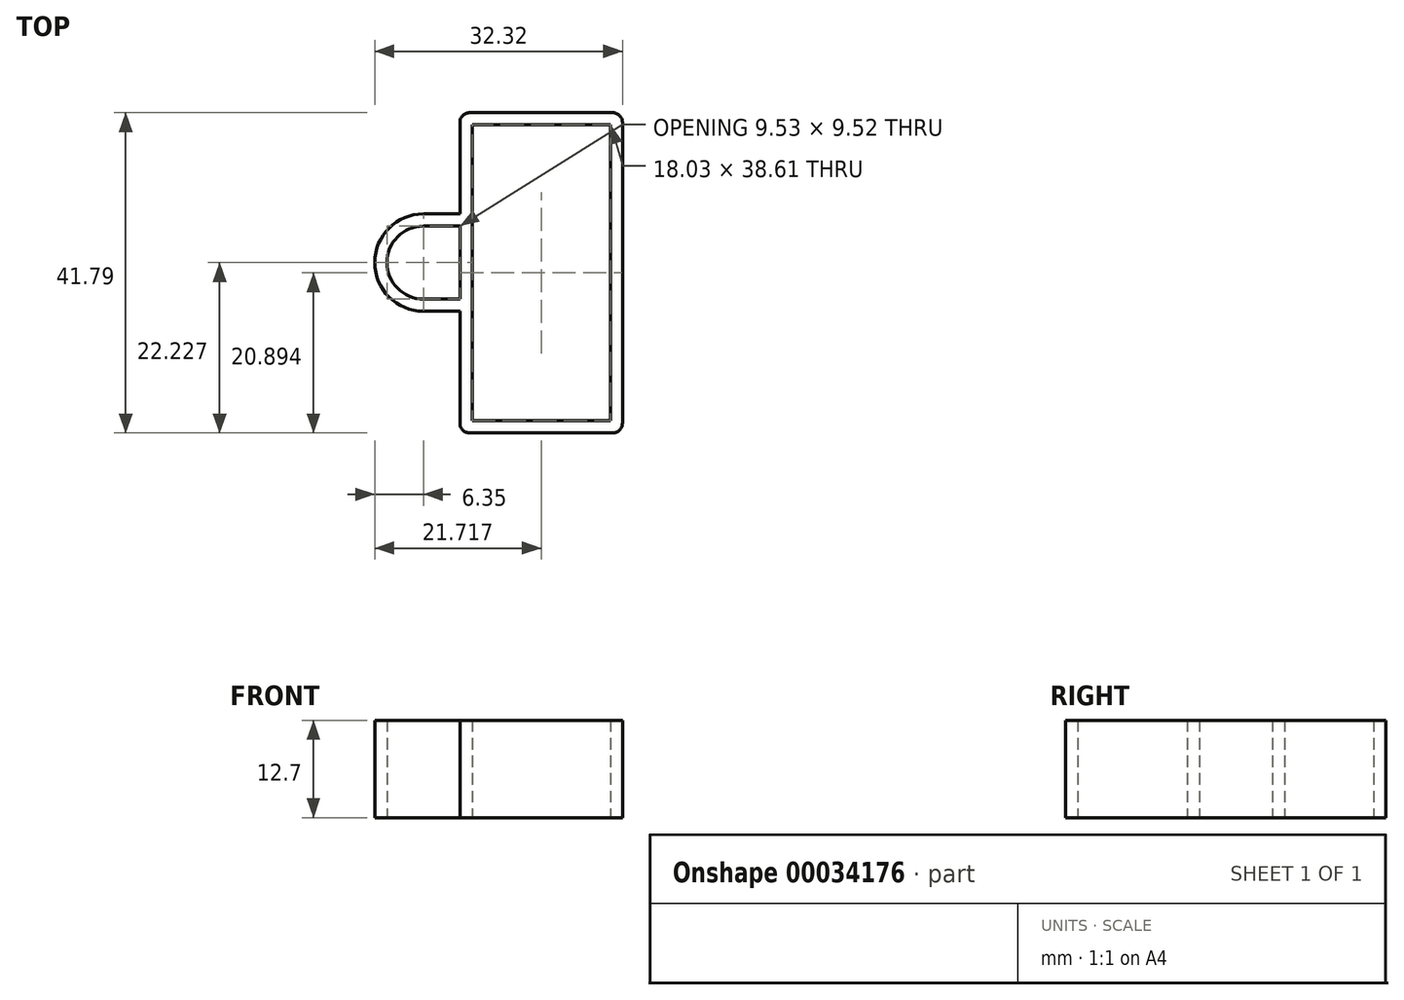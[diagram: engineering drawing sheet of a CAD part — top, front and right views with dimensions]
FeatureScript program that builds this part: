
annotation { "Feature Type Name" : "Feature", "Feature Type Description" : "" }
export const myFeature = defineFeature(function(context is Context, id is Id, definition is map)
    precondition{}
    {
        {
            var Q0;
            Q0=qCreatedBy(makeId("Top.planeOp"),FACE);
            var sketch = newSketch(context, id + "F0", { "sketchPlane" : qUnion([Q0])});
            skLineSegment(sketch, "E0.bottom", {"start": v(0, 0) * mm, "end": v(18.03, 0) * mm});
            skLineSegment(sketch, "E0.top", {"start": v(0, 38.6) * mm, "end": v(18.03, 38.6) * mm});
            skLineSegment(sketch, "E0.left", {"start": v(0, 0) * mm, "end": v(0, 38.6) * mm});
            skLineSegment(sketch, "E0.right", {"start": v(18.03, 0) * mm, "end": v(18.03, 38.6) * mm});
            skLineSegment(sketch, "E1.0", {"start": v(-1.59, -1.59) * mm, "end": v(-1.59, 40.2) * mm});
            skLineSegment(sketch, "E1.1", {"start": v(-1.59, -1.59) * mm, "end": v(19.62, -1.59) * mm});
            skLineSegment(sketch, "E1.2", {"start": v(19.62, -1.59) * mm, "end": v(19.62, 40.2) * mm});
            skLineSegment(sketch, "E1.3", {"start": v(-1.59, 40.2) * mm, "end": v(19.62, 40.2) * mm});
            skArc(sketch, "E2", {"start": v(-6.35, 25.4) * mm, "mid": v(-11.11, 20.64) * mm, "end": v(-6.35, 15.88) * mm});
            skLineSegment(sketch, "E3", {"start": v(-1.59, 25.4) * mm, "end": v(-6.35, 25.4) * mm});
            skLineSegment(sketch, "E4", {"start": v(-1.59, 15.88) * mm, "end": v(-6.35, 15.88) * mm});
            skLineSegment(sketch, "E5.0", {"start": v(-1.59, 14.29) * mm, "end": v(-6.35, 14.29) * mm});
            skArc(sketch, "E5.1", {"start": v(-6.35, 26.99) * mm, "mid": v(-12.7, 20.64) * mm, "end": v(-6.35, 14.29) * mm});
            skLineSegment(sketch, "E5.2", {"start": v(-1.59, 26.99) * mm, "end": v(-6.35, 26.99) * mm});
            skSolve(sketch);
        }
        {
            var Q0;
            Q0=makeQuery(id+"F0.imprint","IMPRINT",FACE,{"disambiguationData":[TD([[makeQuery(id+"F0.imprint","IMPRINT",EDGE,{"derivedFrom":sQuery(id+"F0.wireOp",EDGE,"E0.bottom")}),-1.0]])]});
            var Q1;
            Q1=makeQuery(id+"F0.imprint","IMPRINT",FACE,{"disambiguationData":[TD([[makeQuery(id+"F0.imprint","IMPRINT",EDGE,{"derivedFrom":sQuery(id+"F0.wireOp",EDGE,"E2")}),-1.0]])]});
            extrude(context, id + "F1", {"entities" : qUnion([Q0, Q1]), "depth" : 12.7 * mm});
        }
        {
            var Q0;
            Q0=makeQuery(id+"F1.opExtrude","SWEPT_EDGE",EDGE,{"disambiguationData":[OSD([sQuery(id+"F0.wireOp",EDGE,"E1.1"),sQuery(id+"F0.wireOp",EDGE,"E1.2")])]});
            var Q1;
            Q1=makeQuery(id+"F1.opExtrude","SWEPT_EDGE",EDGE,{"disambiguationData":[OSD([sQuery(id+"F0.wireOp",EDGE,"E1.0"),sQuery(id+"F0.wireOp",EDGE,"E1.1")])]});
            var Q2;
            Q2=makeQuery(id+"F1.opExtrude","SWEPT_EDGE",EDGE,{"disambiguationData":[OSD([sQuery(id+"F0.wireOp",EDGE,"E1.0"),sQuery(id+"F0.wireOp",EDGE,"E1.3")])]});
            var Q3;
            Q3=makeQuery(id+"F1.opExtrude","SWEPT_EDGE",EDGE,{"disambiguationData":[OSD([sQuery(id+"F0.wireOp",EDGE,"E1.2"),sQuery(id+"F0.wireOp",EDGE,"E1.3")])]});
            fillet(context, id + "F2", {"entities" : qUnion([Q0, Q1, Q2, Q3]), "radius" : 1.27 * mm, "tangentPropagation" : true, "allowEdgeOverflow" : false});
        }
    });
